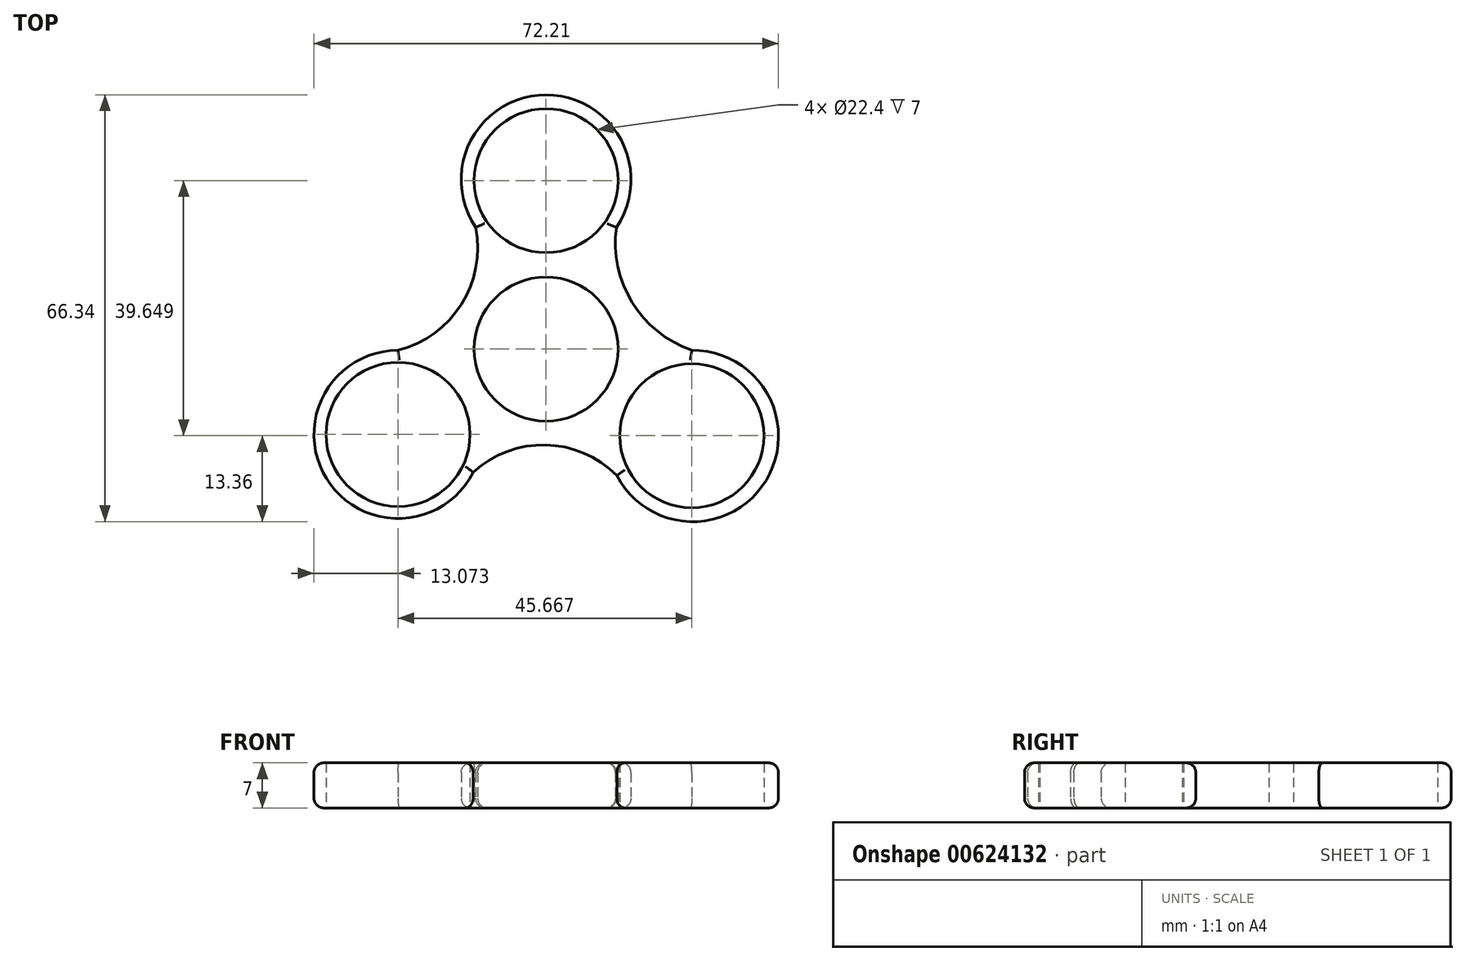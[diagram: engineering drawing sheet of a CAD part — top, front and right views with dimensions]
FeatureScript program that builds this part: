
annotation { "Feature Type Name" : "Feature", "Feature Type Description" : "" }
export const myFeature = defineFeature(function(context is Context, id is Id, definition is map)
    precondition{}
    {
        {
            var Q0;
            Q0=qCreatedBy(makeId("Top.planeOp"),FACE);
            var sketch = newSketch(context, id + "F0", { "sketchPlane" : qUnion([Q0])});
            skCircle(sketch, "E0", {"center": v(0, 0) * mm, "radius": 11.2 * mm});
            skCircle(sketch, "E1", {"center": v(0, 26.18) * mm, "radius": 11.2 * mm});
            skCircle(sketch, "E2.1.0", {"center": v(-23, -13.27) * mm, "radius": 11.2 * mm});
            skArc(sketch, "E2.1.1", {"start": v(-23, -0.2) * mm, "mid": v(-34.14, -20.12) * mm, "end": v(-11.34, -19.15) * mm});
            skCircle(sketch, "E2.2.0", {"center": v(22.66, -13.47) * mm, "radius": 11.2 * mm});
            skPoint(sketch, "E2.center", {"position": v(-0.12, -0.19) * mm});
            skArc(sketch, "E3", {"start": v(-23, -0.2) * mm, "mid": v(-13.17, 6.96) * mm, "end": v(-10.93, 18.92) * mm});
            skArc(sketch, "E4", {"start": v(10.94, 18.92) * mm, "mid": v(13.39, 7.27) * mm, "end": v(22.66, -0.2) * mm});
            skArc(sketch, "E5", {"start": v(11, -19.66) * mm, "mid": v(-0.07, -14.9) * mm, "end": v(-11.34, -19.15) * mm});
            skArc(sketch, "E6.trimOffspring", {"start": v(10.94, 18.92) * mm, "mid": v(0, 39.51) * mm, "end": v(-10.93, 18.92) * mm});
            skArc(sketch, "E7", {"start": v(11, -19.66) * mm, "mid": v(34.24, -20.36) * mm, "end": v(22.66, -0.2) * mm});
            skSolve(sketch);
        }
        {
            var Q0;
            Q0=makeQuery(id+"F0.imprint","IMPRINT",FACE,{"disambiguationData":[TD([[makeQuery(id+"F0.imprint","IMPRINT",EDGE,{"derivedFrom":sQuery(id+"F0.wireOp",EDGE,"E0")}),-1.0]])]});
            extrude(context, id + "F1", {"entities" : qUnion([Q0]), "depth" : 7 * mm, "offsetDistance" : 25 * mm});
        }
        {
            var Q0;
            Q0=makeQuery(id+"F1.opExtrude","CAP_EDGE",EDGE,{"disambiguationData":[OSD([sQuery(id+"F0.wireOp",EDGE,"E5")])],"isStart":false});
            var Q1;
            Q1=makeQuery(id+"F1.opExtrude","CAP_EDGE",EDGE,{"disambiguationData":[OSD([sQuery(id+"F0.wireOp",EDGE,"E5")])],"isStart":true});
            var Q2;
            Q2=makeQuery(id+"F1.opExtrude","CAP_EDGE",EDGE,{"disambiguationData":[OSD([sQuery(id+"F0.wireOp",EDGE,"E2.1.1")])],"isStart":false});
            var Q3;
            Q3=makeQuery(id+"F1.opExtrude","CAP_EDGE",EDGE,{"disambiguationData":[OSD([sQuery(id+"F0.wireOp",EDGE,"E3")])],"isStart":false});
            var Q4;
            Q4=makeQuery(id+"F1.opExtrude","CAP_EDGE",EDGE,{"disambiguationData":[OSD([sQuery(id+"F0.wireOp",EDGE,"E6.trimOffspring")])],"isStart":false});
            var Q5;
            Q5=makeQuery(id+"F1.opExtrude","CAP_EDGE",EDGE,{"disambiguationData":[OSD([sQuery(id+"F0.wireOp",EDGE,"E4")])],"isStart":false});
            var Q6;
            Q6=makeQuery(id+"F1.opExtrude","CAP_EDGE",EDGE,{"disambiguationData":[OSD([sQuery(id+"F0.wireOp",EDGE,"E7")])],"isStart":false});
            fillet(context, id + "F2", {"entities" : qUnion([Q0, Q1, Q2, Q3, Q4, Q5, Q6]), "radius" : 1.5 * mm, "tangentPropagation" : true, "allowEdgeOverflow" : false});
        }
        {
            var Q0;
            Q0=makeQuery(id+"F1.opExtrude","CAP_EDGE",EDGE,{"disambiguationData":[OSD([sQuery(id+"F0.wireOp",EDGE,"E7")])],"isStart":true});
            var Q1;
            {var subQ0=sQuery(id+"F0.wireOp",EDGE,"E5");Q1=makeQuery(id+"F2.opFillet","BLEND_EDGE",EDGE,{"blendedFrom":[makeQuery(id+"F1.opExtrude","CAP_EDGE",EDGE,{"disambiguationData":[OSD([subQ0])],"isStart":true}),makeQuery(id+"F1.opExtrude","CAP_FACE",FACE,{"disambiguationData":[OSD([sQuery(id+"F0.wireOp",EDGE,"E0"),sQuery(id+"F0.wireOp",EDGE,"E1"),sQuery(id+"F0.wireOp",EDGE,"E2.1.0"),sQuery(id+"F0.wireOp",EDGE,"E2.1.1"),sQuery(id+"F0.wireOp",EDGE,"E2.2.0"),sQuery(id+"F0.wireOp",EDGE,"E3"),sQuery(id+"F0.wireOp",EDGE,"E4"),subQ0,sQuery(id+"F0.wireOp",EDGE,"E6.trimOffspring"),sQuery(id+"F0.wireOp",EDGE,"E7")])],"isStart":true})],"blendedInto":[makeQuery(id+"F1.opExtrude","CAP_FACE",FACE,{"disambiguationData":[OSD([sQuery(id+"F0.wireOp",EDGE,"E0"),sQuery(id+"F0.wireOp",EDGE,"E1"),sQuery(id+"F0.wireOp",EDGE,"E2.1.0"),sQuery(id+"F0.wireOp",EDGE,"E2.1.1"),sQuery(id+"F0.wireOp",EDGE,"E2.2.0"),sQuery(id+"F0.wireOp",EDGE,"E3"),sQuery(id+"F0.wireOp",EDGE,"E4"),subQ0,sQuery(id+"F0.wireOp",EDGE,"E6.trimOffspring"),sQuery(id+"F0.wireOp",EDGE,"E7")])],"isStart":true})]});}
            var Q2;
            Q2=makeQuery(id+"F1.opExtrude","CAP_EDGE",EDGE,{"disambiguationData":[OSD([sQuery(id+"F0.wireOp",EDGE,"E2.1.1")])],"isStart":true});
            var Q3;
            Q3=makeQuery(id+"F1.opExtrude","CAP_EDGE",EDGE,{"disambiguationData":[OSD([sQuery(id+"F0.wireOp",EDGE,"E3")])],"isStart":true});
            var Q4;
            Q4=makeQuery(id+"F1.opExtrude","CAP_EDGE",EDGE,{"disambiguationData":[OSD([sQuery(id+"F0.wireOp",EDGE,"E6.trimOffspring")])],"isStart":true});
            var Q5;
            Q5=makeQuery(id+"F1.opExtrude","CAP_EDGE",EDGE,{"disambiguationData":[OSD([sQuery(id+"F0.wireOp",EDGE,"E4")])],"isStart":true});
            fillet(context, id + "F3", {"entities" : qUnion([Q0, Q1, Q2, Q3, Q4, Q5]), "radius" : 1.5 * mm, "tangentPropagation" : true, "allowEdgeOverflow" : false});
        }
    });
